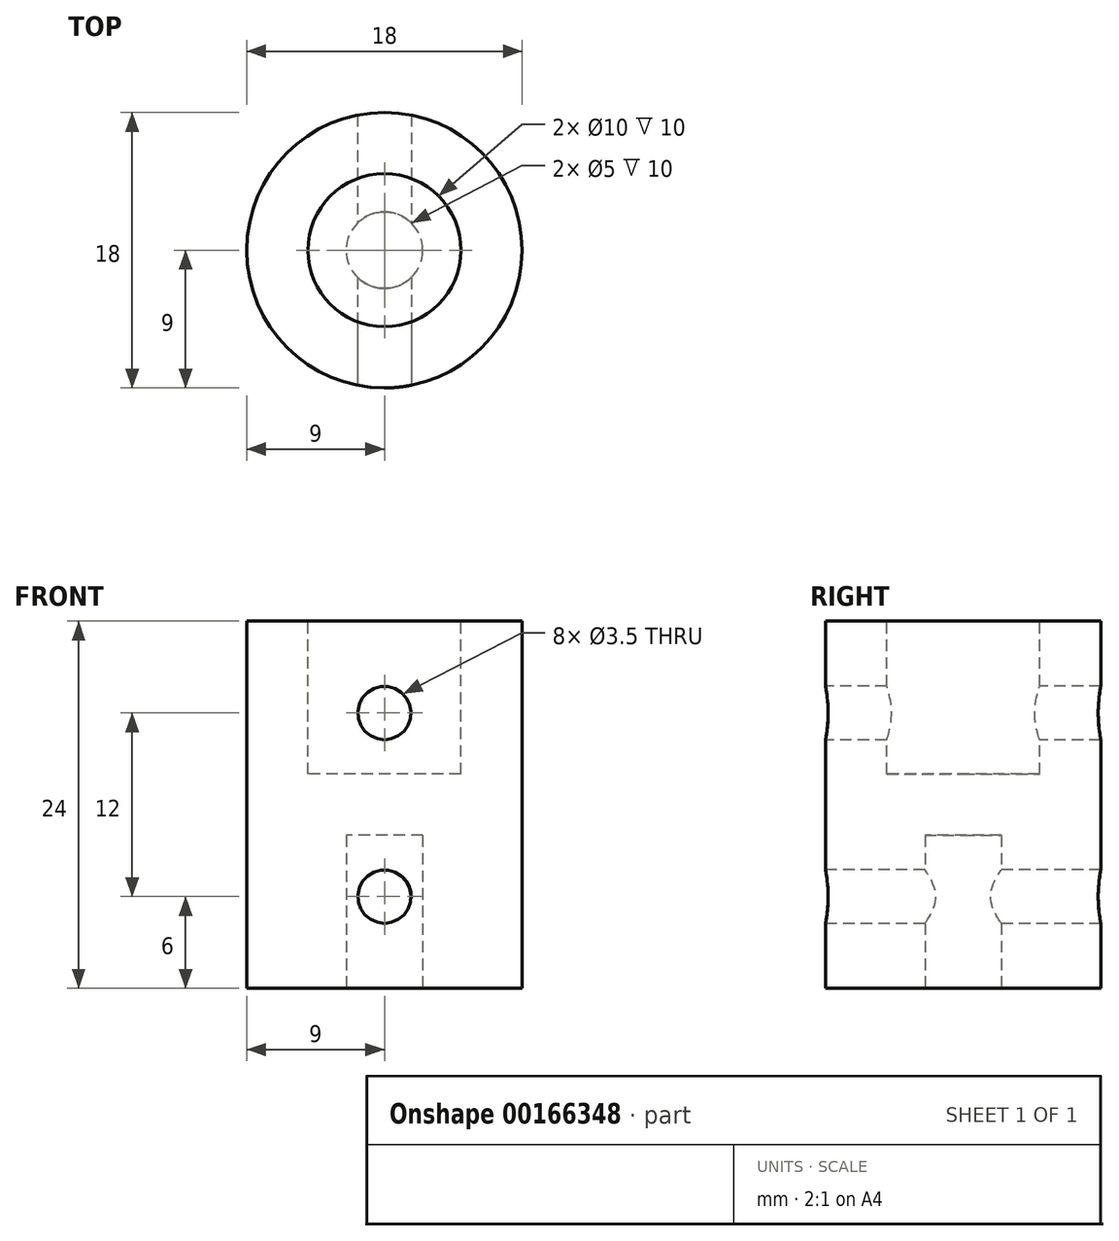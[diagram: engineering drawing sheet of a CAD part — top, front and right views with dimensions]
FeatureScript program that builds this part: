
annotation { "Feature Type Name" : "Feature", "Feature Type Description" : "" }
export const myFeature = defineFeature(function(context is Context, id is Id, definition is map)
    precondition{}
    {
        {
            var Q0;
            Q0=qCreatedBy(makeId("Top.planeOp"),FACE);
            var sketch = newSketch(context, id + "F0", { "sketchPlane" : qUnion([Q0])});
            skCircle(sketch, "E0", {"center": v(0, 0) * mm, "radius": 9 * mm});
            skSolve(sketch);
        }
        {
            var Q0;
            Q0 = qSketchRegion(id + "F0", true);
            extrude(context, id + "F1", {"entities" : qUnion([Q0]), "depth" : 24 * mm});
        }
        {
            var Q0;
            Q0=makeQuery(id+"F1.opExtrude","CAP_FACE",FACE,{"disambiguationData":[OSD([sQuery(id+"F0.wireOp",EDGE,"E0")])],"isStart":false});
            var sketch = newSketch(context, id + "F2", { "sketchPlane" : qUnion([Q0])});
            skCircle(sketch, "E1", {"center": v(0, 0) * mm, "radius": 5 * mm});
            skSolve(sketch);
        }
        {
            var Q0;
            Q0 = qSketchRegion(id + "F2", true);
            extrude(context, id + "F3", {"entities" : qUnion([Q0]), "operationType" : NewBodyOperationType.REMOVE, "oppositeDirection" : true, "depth" : 10 * mm});
        }
        {
            var Q0;
            Q0=qCreatedBy(makeId("Top.planeOp"),FACE);
            var sketch = newSketch(context, id + "F4", { "sketchPlane" : qUnion([Q0])});
            skCircle(sketch, "E2", {"center": v(0, 0) * mm, "radius": 2.5 * mm});
            skSolve(sketch);
        }
        {
            var Q0;
            Q0=makeQuery(id+"F4.imprint","IMPRINT",FACE,{"disambiguationData":[TD([[makeQuery(id+"F4.imprint","IMPRINT",EDGE,{"derivedFrom":sQuery(id+"F4.wireOp",EDGE,"E2")}),1.0]])]});
            extrude(context, id + "F5", {"entities" : qUnion([Q0]), "operationType" : NewBodyOperationType.REMOVE, "depth" : 10 * mm});
        }
        {
            var Q0;
            Q0=qCreatedBy(makeId("Front.planeOp"),FACE);
            var sketch = newSketch(context, id + "F6", { "sketchPlane" : qUnion([Q0])});
            skLineSegment(sketch, "E3", {"start": v(0, 0) * mm, "end": v(0, 6) * mm});
            skCircle(sketch, "E4", {"center": v(0, 6) * mm, "radius": 1.75 * mm});
            skLineSegment(sketch, "E5", {"start": v(0, 6) * mm, "end": v(0, 18) * mm});
            skCircle(sketch, "E6", {"center": v(0, 18) * mm, "radius": 1.75 * mm});
            skSolve(sketch);
        }
        {
            var Q0;
            Q0 = qSketchRegion(id + "F6", true);
            extrude(context, id + "F7", {"entities" : qUnion([Q0]), "operationType" : NewBodyOperationType.REMOVE, "oppositeDirection" : true, "depth" : 25 * mm, "hasSecondDirection" : true, "secondDirectionOppositeDirection" : false, "secondDirectionDepth" : 25 * mm});
        }
    });
